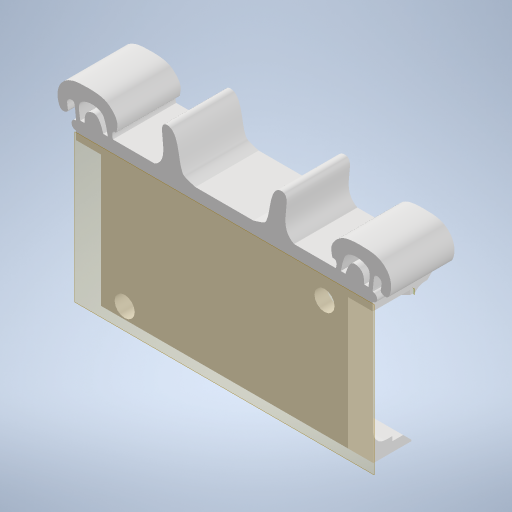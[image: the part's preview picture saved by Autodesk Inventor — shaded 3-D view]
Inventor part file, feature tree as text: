
AUTODESK INVENTOR PART (.ipt)
format: ipt  version: 2023 (Build 270158030, 158C)  size: 428,032 bytes
history: native  units: mm
features: other x5, extrude x5, sketch x5, chamfer x4, fillet x3, plane x2, reference x1
ambient origin geometry x8: Origin, YZ Plane, XZ Plane, XY Plane, X Axis, Y Axis, Z Axis, Center Point
bodies: Solid1 (feature_tree)
feature tree (25):
  other  "Blocks"
  extrude  "Extrusion1"  Depth=2.0mm
  plane  "Work Plane1"
  extrude  "Extrusion2"  Depth=10.0mm TaperAngle=0.0deg
  extrude  "Extrusion3"  Depth=10.0mm
  chamfer  "Chamfer1"  Distance=2.0mm Angle=45.0deg
  chamfer  "Chamfer2"  Distance=2.0mm Angle=45.0deg
  chamfer  "Chamfer3"  Distance=2.0mm Angle=45.0deg
  extrude  "Extrusion4"  Depth=2.0mm
  chamfer  "Chamfer4"  Distance=1.0mm
  fillet  "Fillet1"  Radius=5.0mm
  plane  "Work Plane2"
  extrude  "Extrusion5"  Depth=2.0mm TaperAngle=45.0deg
  fillet  "Fillet2"  Radius=2.0mm
  fillet  "Fillet3"  Radius=1.35mm
  sketch  "Sketch1"  dims[d0=2.0mm d1=0.0mm d2=1.908101mm]
  reference  "Reference1"
  sketch  "Sketch2"  dims[d3=1.985343mm d4=10.0mm d5=0.0mm]
  other  "DIN-rail-mount"
  sketch  "Sketch3"  dims[d6=10.0mm d7=0.0mm d8=8.0mm]
  sketch  "Sketch4"  dims[d9=1.5mm]
  sketch  "Sketch5"  dims[d10=0.7mm d11=2.0mm d12=2.0mm d13=45.0deg d14=1.3mm d15=2.0mm d16=45.0deg d17=1.4mm d18=2.0mm d19=45.0deg d20=1.7mm d21=1.0mm d22=5.0mm d23=0.0mm d24=1.9mm d25=2.0mm d26=45.0deg d27=2.0mm d28=1.35mm d29=5.0mm d30=6.0mm d31=4.0mm d32=2.0mm d33=3.0mm d34=0.2mm d35=0.8mm d36=0.8mm d37=10.0mm d38=-1.047198mm d39=2.0mm d40=2.0mm]
  other  "buck-converter-din-rail-mount.iam"
  other  "Power Buck Converter:1"
  other  "DIN-rail-mount:1"
